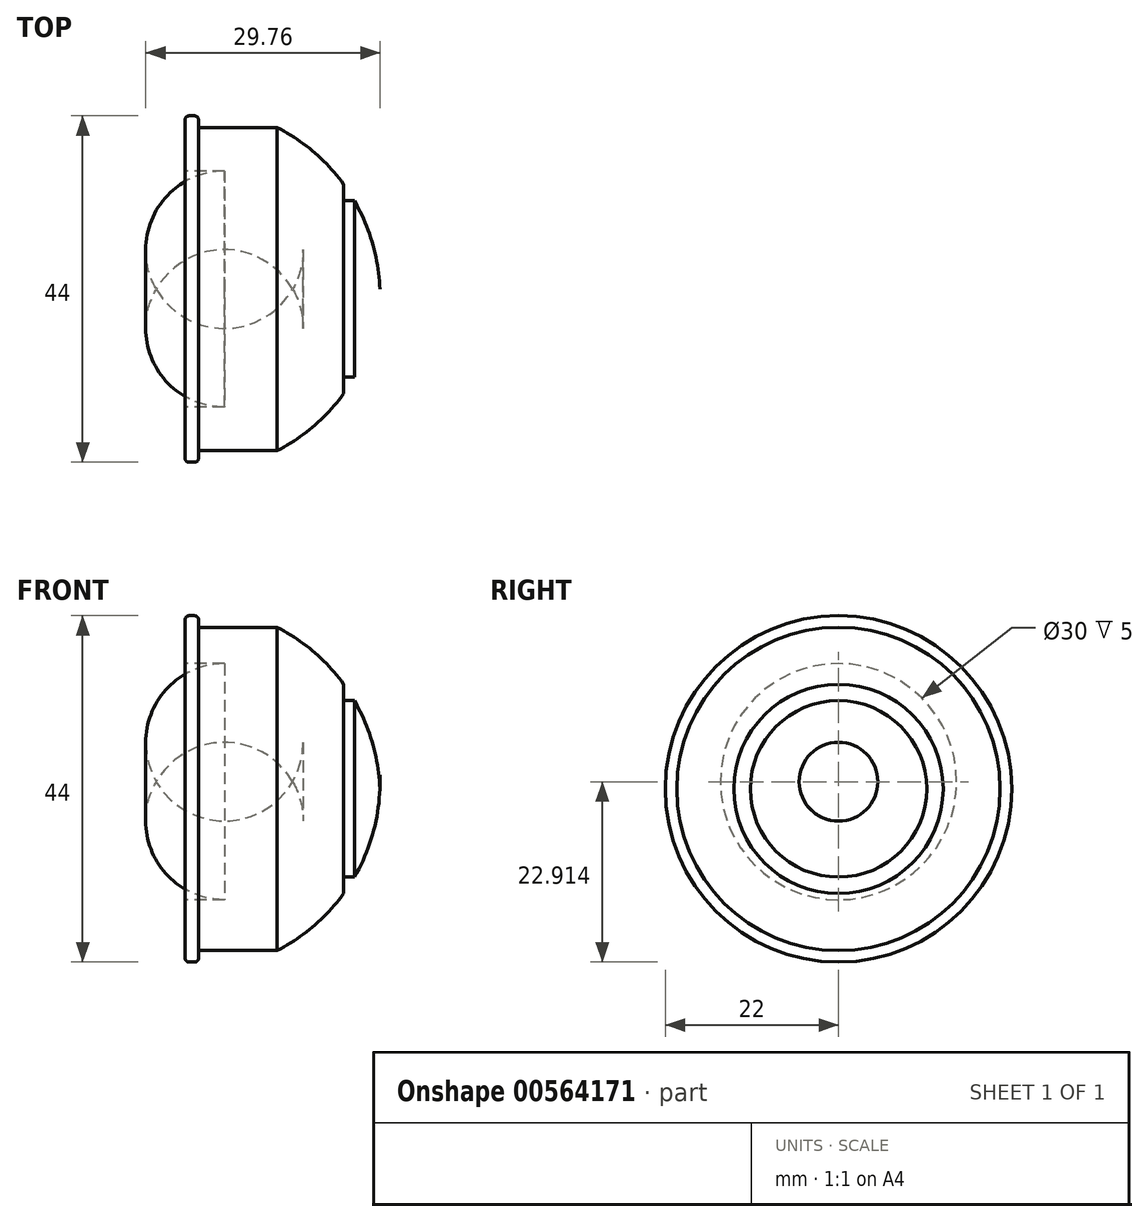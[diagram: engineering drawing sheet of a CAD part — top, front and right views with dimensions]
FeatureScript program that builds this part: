
annotation { "Feature Type Name" : "Feature", "Feature Type Description" : "" }
export const myFeature = defineFeature(function(context is Context, id is Id, definition is map)
    precondition{}
    {
        {
            var Q0;
            Q0=qCreatedBy(makeId("Right.planeOp"),FACE);
            var sketch = newSketch(context, id + "F0", { "sketchPlane" : qUnion([Q0])});
            skCircle(sketch, "E0", {"center": v(0, 0) * mm, "radius": 20.5 * mm});
            skSolve(sketch);
        }
        {
            var Q0;
            Q0 = qSketchRegion(id + "F0", true);
            extrude(context, id + "F1", {"entities" : qUnion([Q0]), "depth" : 10 * mm, "offsetDistance" : 25 * mm});
        }
        {
            var Q0;
            Q0=qCreatedBy(makeId("Front.planeOp"),FACE);
            var sketch = newSketch(context, id + "F2", { "sketchPlane" : qUnion([Q0])});
            skArc(sketch, "E1", {"start": v(23.04, 0) * mm, "mid": v(22.11, 5.8) * mm, "end": v(19.8, 11.2) * mm});
            skLineSegment(sketch, "E2", {"start": v(10, 0) * mm, "end": v(10, 20.53) * mm});
            skLineSegment(sketch, "E3", {"start": v(-74.94, 0) * mm, "end": v(97.62, 0) * mm, "construction": true});
            skLineSegment(sketch, "E4", {"start": v(23.04, 0) * mm, "end": v(10, 0) * mm});
            skLineSegment(sketch, "E5", {"start": v(18.44, 13.3) * mm, "end": v(18.44, 11.2) * mm});
            skLineSegment(sketch, "E6", {"start": v(18.44, 11.2) * mm, "end": v(19.8, 11.2) * mm});
            skArc(sketch, "E7.trimOffspring", {"start": v(18.44, 13.3) * mm, "mid": v(14.65, 17.4) * mm, "end": v(10, 20.53) * mm});
            skSolve(sketch);
        }
        {
            var Q0;
            Q0=makeQuery(id+"F2.imprint","IMPRINT",FACE,{"disambiguationData":[TD([[makeQuery(id+"F2.imprint","IMPRINT",EDGE,{"derivedFrom":sQuery(id+"F2.wireOp",EDGE,"E1")}),1.0]])]});
            var Q1;
            Q1=sQuery(id+"F2.wireOp",EDGE,"E3");
            revolve(context, id + "F3", {"operationType" : NewBodyOperationType.ADD, "entities" : qUnion([Q0]), "axis" : qUnion([Q1]), "revolveType" : RevolveType.FULL});
        }
        {
            var Q0;
            Q0=makeQuery(id+"F1.opExtrude","CAP_FACE",FACE,{"disambiguationData":[OSD([sQuery(id+"F0.wireOp",EDGE,"E0")])],"isStart":true});
            var sketch = newSketch(context, id + "F4", { "sketchPlane" : qUnion([Q0])});
            skCircle(sketch, "E8", {"center": v(0, 0) * mm, "radius": 22 * mm});
            skSolve(sketch);
        }
        {
            var Q0;
            Q0 = qSketchRegion(id + "F4", true);
            extrude(context, id + "F5", {"entities" : qUnion([Q0]), "operationType" : NewBodyOperationType.ADD, "depth" : 1.7 * mm, "offsetDistance" : 25 * mm});
        }
        {
            var Q0;
            Q0=makeQuery(id+"F5.opExtrude","CAP_EDGE",EDGE,{"disambiguationData":[OSD([sQuery(id+"F4.wireOp",EDGE,"E8")])],"isStart":false});
            var Q1;
            Q1=makeQuery(id+"F5.opExtrude","CAP_EDGE",EDGE,{"disambiguationData":[OSD([sQuery(id+"F4.wireOp",EDGE,"E8")])],"isStart":true});
            fillet(context, id + "F6", {"entities" : qUnion([Q0, Q1]), "radius" : .5 * mm, "tangentPropagation" : true, "allowEdgeOverflow" : false});
        }
        {
            var Q0;
            Q0=makeQuery(id+"F5.opExtrude","CAP_FACE",FACE,{"disambiguationData":[OSD([sQuery(id+"F4.wireOp",EDGE,"E8")])],"isStart":false});
            var sketch = newSketch(context, id + "F7", { "sketchPlane" : qUnion([Q0])});
            skCircle(sketch, "E9", {"center": v(0, 0.91) * mm, "radius": 15 * mm});
            skSolve(sketch);
        }
        {
            var Q0;
            Q0 = qSketchRegion(id + "F7", true);
            extrude(context, id + "F8", {"entities" : qUnion([Q0]), "operationType" : NewBodyOperationType.REMOVE, "oppositeDirection" : true, "depth" : 15 * mm, "offsetDistance" : 25 * mm});
        }
        {
            var Q0;
            Q0=makeQuery(id+"F8.boolean.opBoolean","COPY",EDGE,{"derivedFrom":makeQuery(id+"F8.opExtrude","CAP_EDGE",EDGE,{"disambiguationData":[OSD([sQuery(id+"F7.wireOp",EDGE,"E9")])],"isStart":false})});
            fillet(context, id + "F9", {"entities" : qUnion([Q0]), "radius" : 10 * mm, "tangentPropagation" : true, "allowEdgeOverflow" : false});
        }
    });
